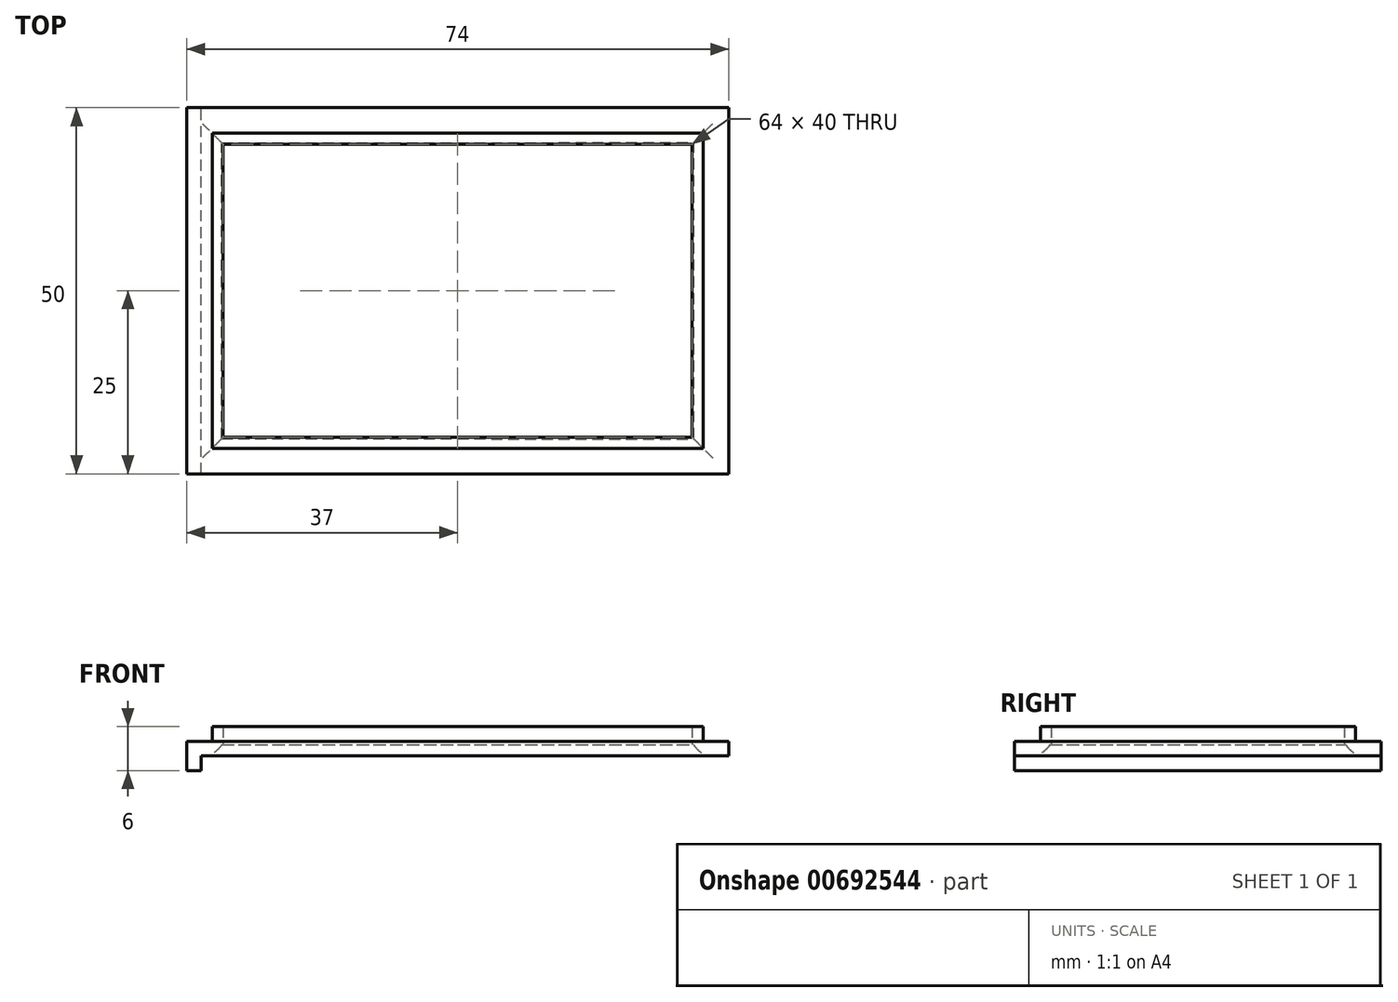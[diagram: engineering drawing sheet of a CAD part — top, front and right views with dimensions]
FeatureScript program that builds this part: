
annotation { "Feature Type Name" : "Feature", "Feature Type Description" : "" }
export const myFeature = defineFeature(function(context is Context, id is Id, definition is map)
    precondition{}
    {
        {
            var Q0;
            Q0=qCreatedBy(makeId("Front.planeOp"),FACE);
            var sketch = newSketch(context, id + "F0", { "sketchPlane" : qUnion([Q0])});
            skPoint(sketch, "E0", {"position": v(2, 2) * mm});
            skLineSegment(sketch, "E1", {"start": v(2, 2) * mm, "end": v(74, 2) * mm});
            skPoint(sketch, "E2", {"position": v(2, 0) * mm});
            skLineSegment(sketch, "E3", {"start": v(0, 0) * mm, "end": v(2, 0) * mm});
            skLineSegment(sketch, "E4", {"start": v(74, 2) * mm, "end": v(74, -3.85) * mm});
            skPoint(sketch, "E5", {"position": v(4, 2) * mm});
            skPoint(sketch, "E6", {"position": v(0, 2) * mm});
            skPoint(sketch, "E7", {"position": v(6, 2) * mm});
            skPoint(sketch, "E8", {"position": v(0, 3.96) * mm});
            skLineSegment(sketch, "E9", {"start": v(0, 3.96) * mm, "end": v(0, 0) * mm});
            skLineSegment(sketch, "E10", {"start": v(2, 0) * mm, "end": v(2, 2) * mm});
            skLineSegment(sketch, "E11", {"start": v(74, 4) * mm, "end": v(74, 2) * mm});
            skLineSegment(sketch, "E12", {"start": v(0, 3.96) * mm, "end": v(74, 4) * mm});
            skSolve(sketch);
        }
        {
            var Q0;
            Q0=makeQuery(id+"F0.imprint","IMPRINT",FACE,{"disambiguationData":[TD([[makeQuery(id+"F0.imprint","IMPRINT",EDGE,{"derivedFrom":sQuery(id+"F0.wireOp",EDGE,"E1")}),1.0]])]});
            extrude(context, id + "F1", {"entities" : qUnion([Q0]), "depth" : 50 * mm, "offsetDistance" : 25 * mm});
        }
        {
            var Q0;
            Q0=qCreatedBy(makeId("Top.planeOp"),FACE);
            var sketch = newSketch(context, id + "F2", { "sketchPlane" : qUnion([Q0])});
            skLineSegment(sketch, "E13.bottom", {"start": v(5, -45) * mm, "end": v(69, -45) * mm});
            skLineSegment(sketch, "E13.top", {"start": v(5, -5) * mm, "end": v(69, -5) * mm});
            skLineSegment(sketch, "E13.left", {"start": v(5, -45) * mm, "end": v(5, -5) * mm});
            skLineSegment(sketch, "E13.right", {"start": v(69, -45) * mm, "end": v(69, -5) * mm});
            skLineSegment(sketch, "E14.bottom", {"start": v(3.5, -3.5) * mm, "end": v(70.5, -3.5) * mm});
            skLineSegment(sketch, "E14.top", {"start": v(3.5, -46.5) * mm, "end": v(70.5, -46.5) * mm});
            skLineSegment(sketch, "E14.left", {"start": v(3.5, -3.5) * mm, "end": v(3.5, -46.5) * mm});
            skLineSegment(sketch, "E14.right", {"start": v(70.5, -3.5) * mm, "end": v(70.5, -46.5) * mm});
            skSolve(sketch);
        }
        {
            var Q0;
            Q0=makeQuery(id+"F2.imprint","IMPRINT",FACE,{"disambiguationData":[TD([[makeQuery(id+"F2.imprint","IMPRINT",EDGE,{"derivedFrom":sQuery(id+"F2.wireOp",EDGE,"E13.bottom")}),1.0]])]});
            var Q1;
            Q1=makeQuery(id+"F1.opExtrude","SWEPT_FACE",FACE,{"disambiguationData":[OSD([sQuery(id+"F0.wireOp",EDGE,"E12")])]});
            extrude(context, id + "F3", {"entities" : qUnion([Q0, Q1]), "operationType" : NewBodyOperationType.REMOVE, "depth" : 25 * mm, "offsetDistance" : 25 * mm});
        }
        {
            var Q0;
            Q0=makeQuery(id+"F3.boolean.opBoolean","INTERSECT",EDGE,{"derivedFrom":[makeQuery(id+"F1.opExtrude","SWEPT_FACE",FACE,{"disambiguationData":[OSD([sQuery(id+"F0.wireOp",EDGE,"E1")])]}),makeQuery(id+"F3.opExtrude","SWEPT_FACE",FACE,{"disambiguationData":[OSD([sQuery(id+"F2.wireOp",EDGE,"E13.left")])]})]});
            var Q1;
            Q1=makeQuery(id+"F3.boolean.opBoolean","INTERSECT",EDGE,{"derivedFrom":[makeQuery(id+"F1.opExtrude","SWEPT_FACE",FACE,{"disambiguationData":[OSD([sQuery(id+"F0.wireOp",EDGE,"E1")])]}),makeQuery(id+"F3.opExtrude","SWEPT_FACE",FACE,{"disambiguationData":[OSD([sQuery(id+"F2.wireOp",EDGE,"E13.bottom")])]})]});
            var Q2;
            Q2=makeQuery(id+"F3.boolean.opBoolean","INTERSECT",EDGE,{"derivedFrom":[makeQuery(id+"F1.opExtrude","SWEPT_FACE",FACE,{"disambiguationData":[OSD([sQuery(id+"F0.wireOp",EDGE,"E1")])]}),makeQuery(id+"F3.opExtrude","SWEPT_FACE",FACE,{"disambiguationData":[OSD([sQuery(id+"F2.wireOp",EDGE,"E13.right")])]})]});
            var Q3;
            Q3=makeQuery(id+"F3.boolean.opBoolean","INTERSECT",EDGE,{"derivedFrom":[makeQuery(id+"F1.opExtrude","SWEPT_FACE",FACE,{"disambiguationData":[OSD([sQuery(id+"F0.wireOp",EDGE,"E1")])]}),makeQuery(id+"F3.opExtrude","SWEPT_FACE",FACE,{"disambiguationData":[OSD([sQuery(id+"F2.wireOp",EDGE,"E13.top")])]})]});
            fillet(context, id + "F4", {"entities" : qUnion([Q0, Q1, Q2, Q3]), "radius" : 3 * mm, "tangentPropagation" : true, "allowEdgeOverflow" : false});
        }
        {
            var Q0;
            Q0 = qSketchRegion(id + "F2", true);
            extrude(context, id + "F5", {"entities" : qUnion([Q0]), "operationType" : NewBodyOperationType.ADD, "depth" : 6 * mm, "offsetDistance" : 25 * mm, "hasSecondDirection" : true, "secondDirectionOppositeDirection" : false, "secondDirectionDepth" : 3.5 * mm});
        }
    });
